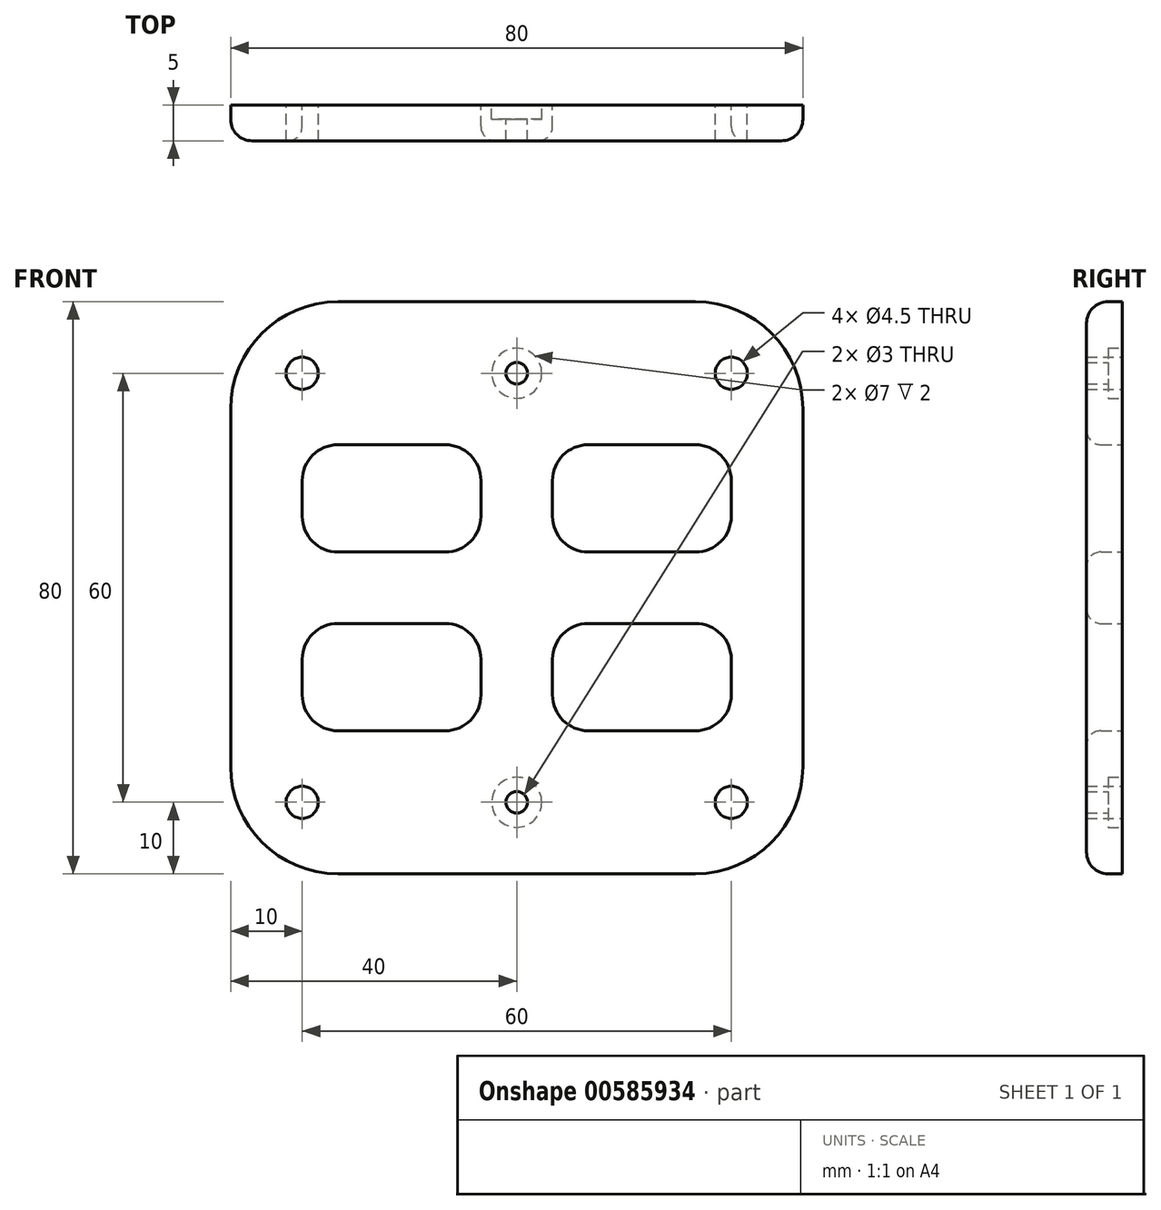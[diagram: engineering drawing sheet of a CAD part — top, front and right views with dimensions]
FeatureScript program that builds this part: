
annotation { "Feature Type Name" : "Feature", "Feature Type Description" : "" }
export const myFeature = defineFeature(function(context is Context, id is Id, definition is map)
    precondition{}
    {
        {
            var Q0;
            Q0=qCreatedBy(makeId("Front.planeOp"),FACE);
            var sketch = newSketch(context, id + "F0", { "sketchPlane" : qUnion([Q0])});
            skLineSegment(sketch, "E0.bottom", {"start": v(-40, 40) * mm, "end": v(40, 40) * mm});
            skLineSegment(sketch, "E0.top", {"start": v(-40, -40) * mm, "end": v(40, -40) * mm});
            skLineSegment(sketch, "E0.left", {"start": v(-40, 40) * mm, "end": v(-40, -40) * mm});
            skLineSegment(sketch, "E0.right", {"start": v(40, 40) * mm, "end": v(40, -40) * mm});
            skCircle(sketch, "E1", {"center": v(-30, 30) * mm, "radius": 2.25 * mm});
            skCircle(sketch, "E2", {"center": v(0, 30) * mm, "radius": 1.5 * mm});
            skCircle(sketch, "E3", {"center": v(30, 30) * mm, "radius": 2.25 * mm});
            skCircle(sketch, "E4", {"center": v(-30, -30) * mm, "radius": 2.25 * mm});
            skCircle(sketch, "E5", {"center": v(0, -30) * mm, "radius": 1.5 * mm});
            skCircle(sketch, "E6", {"center": v(30, -30) * mm, "radius": 2.25 * mm});
            skLineSegment(sketch, "E7.bottom", {"start": v(-30, 20) * mm, "end": v(-5, 20) * mm});
            skLineSegment(sketch, "E7.top", {"start": v(-30, 5) * mm, "end": v(-5, 5) * mm});
            skLineSegment(sketch, "E7.left", {"start": v(-30, 20) * mm, "end": v(-30, 5) * mm});
            skLineSegment(sketch, "E7.right", {"start": v(-5, 20) * mm, "end": v(-5, 5) * mm});
            skLineSegment(sketch, "E8.bottom", {"start": v(-30, -5) * mm, "end": v(-5, -5) * mm});
            skLineSegment(sketch, "E8.top", {"start": v(-30, -20) * mm, "end": v(-5, -20) * mm});
            skLineSegment(sketch, "E8.left", {"start": v(-30, -5) * mm, "end": v(-30, -20) * mm});
            skLineSegment(sketch, "E8.right", {"start": v(-5, -5) * mm, "end": v(-5, -20) * mm});
            skLineSegment(sketch, "E9.bottom", {"start": v(5, -5) * mm, "end": v(30, -5) * mm});
            skLineSegment(sketch, "E9.top", {"start": v(5, -20) * mm, "end": v(30, -20) * mm});
            skLineSegment(sketch, "E9.left", {"start": v(5, -5) * mm, "end": v(5, -20) * mm});
            skLineSegment(sketch, "E9.right", {"start": v(30, -5) * mm, "end": v(30, -20) * mm});
            skLineSegment(sketch, "E10.bottom", {"start": v(5, 20) * mm, "end": v(30, 20) * mm});
            skLineSegment(sketch, "E10.top", {"start": v(5, 5) * mm, "end": v(30, 5) * mm});
            skLineSegment(sketch, "E10.left", {"start": v(5, 20) * mm, "end": v(5, 5) * mm});
            skLineSegment(sketch, "E10.right", {"start": v(30, 20) * mm, "end": v(30, 5) * mm});
            skSolve(sketch);
        }
        {
            var Q0;
            Q0 = qSketchRegion(id + "F0", true);
            extrude(context, id + "F1", {"entities" : qUnion([Q0]), "depth" : 5 * mm, "offsetDistance" : 25 * mm});
        }
        {
            var Q0;
            Q0=makeQuery(id+"F1.opExtrude","SWEPT_EDGE",EDGE,{"disambiguationData":[OSD([sQuery(id+"F0.wireOp",EDGE,"E10.top"),sQuery(id+"F0.wireOp",EDGE,"E10.right")])]});
            var Q1;
            Q1=makeQuery(id+"F1.opExtrude","SWEPT_EDGE",EDGE,{"disambiguationData":[OSD([sQuery(id+"F0.wireOp",EDGE,"E10.bottom"),sQuery(id+"F0.wireOp",EDGE,"E10.right")])]});
            var Q2;
            Q2=makeQuery(id+"F1.opExtrude","SWEPT_EDGE",EDGE,{"disambiguationData":[OSD([sQuery(id+"F0.wireOp",EDGE,"E10.bottom"),sQuery(id+"F0.wireOp",EDGE,"E10.left")])]});
            var Q3;
            Q3=makeQuery(id+"F1.opExtrude","SWEPT_EDGE",EDGE,{"disambiguationData":[OSD([sQuery(id+"F0.wireOp",EDGE,"E10.top"),sQuery(id+"F0.wireOp",EDGE,"E10.left")])]});
            fillet(context, id + "F2", {"entities" : qUnion([Q0, Q1, Q2, Q3]), "radius" : 5 * mm, "tangentPropagation" : true, "allowEdgeOverflow" : false});
        }
        {
            var Q0;
            Q0=makeQuery(id+"F1.opExtrude","SWEPT_EDGE",EDGE,{"disambiguationData":[OSD([sQuery(id+"F0.wireOp",EDGE,"E7.bottom"),sQuery(id+"F0.wireOp",EDGE,"E7.left")])]});
            var Q1;
            Q1=makeQuery(id+"F1.opExtrude","SWEPT_EDGE",EDGE,{"disambiguationData":[OSD([sQuery(id+"F0.wireOp",EDGE,"E7.top"),sQuery(id+"F0.wireOp",EDGE,"E7.left")])]});
            var Q2;
            Q2=makeQuery(id+"F1.opExtrude","SWEPT_EDGE",EDGE,{"disambiguationData":[OSD([sQuery(id+"F0.wireOp",EDGE,"E7.top"),sQuery(id+"F0.wireOp",EDGE,"E7.right")])]});
            var Q3;
            Q3=makeQuery(id+"F1.opExtrude","SWEPT_EDGE",EDGE,{"disambiguationData":[OSD([sQuery(id+"F0.wireOp",EDGE,"E7.bottom"),sQuery(id+"F0.wireOp",EDGE,"E7.right")])]});
            fillet(context, id + "F3", {"entities" : qUnion([Q0, Q1, Q2, Q3]), "radius" : 5 * mm, "tangentPropagation" : true, "allowEdgeOverflow" : false});
        }
        {
            var Q0;
            Q0=makeQuery(id+"F1.opExtrude","SWEPT_EDGE",EDGE,{"disambiguationData":[OSD([sQuery(id+"F0.wireOp",EDGE,"E8.bottom"),sQuery(id+"F0.wireOp",EDGE,"E8.right")])]});
            var Q1;
            Q1=makeQuery(id+"F1.opExtrude","SWEPT_EDGE",EDGE,{"disambiguationData":[OSD([sQuery(id+"F0.wireOp",EDGE,"E9.bottom"),sQuery(id+"F0.wireOp",EDGE,"E9.right")])]});
            var Q2;
            Q2=makeQuery(id+"F1.opExtrude","SWEPT_EDGE",EDGE,{"disambiguationData":[OSD([sQuery(id+"F0.wireOp",EDGE,"E9.bottom"),sQuery(id+"F0.wireOp",EDGE,"E9.left")])]});
            var Q3;
            Q3=makeQuery(id+"F1.opExtrude","SWEPT_EDGE",EDGE,{"disambiguationData":[OSD([sQuery(id+"F0.wireOp",EDGE,"E8.bottom"),sQuery(id+"F0.wireOp",EDGE,"E8.left")])]});
            var Q4;
            Q4=makeQuery(id+"F1.opExtrude","SWEPT_EDGE",EDGE,{"disambiguationData":[OSD([sQuery(id+"F0.wireOp",EDGE,"E9.top"),sQuery(id+"F0.wireOp",EDGE,"E9.right")])]});
            var Q5;
            Q5=makeQuery(id+"F1.opExtrude","SWEPT_EDGE",EDGE,{"disambiguationData":[OSD([sQuery(id+"F0.wireOp",EDGE,"E8.top"),sQuery(id+"F0.wireOp",EDGE,"E8.right")])]});
            var Q6;
            Q6=makeQuery(id+"F1.opExtrude","SWEPT_EDGE",EDGE,{"disambiguationData":[OSD([sQuery(id+"F0.wireOp",EDGE,"E9.top"),sQuery(id+"F0.wireOp",EDGE,"E9.left")])]});
            var Q7;
            Q7=makeQuery(id+"F1.opExtrude","SWEPT_EDGE",EDGE,{"disambiguationData":[OSD([sQuery(id+"F0.wireOp",EDGE,"E8.top"),sQuery(id+"F0.wireOp",EDGE,"E8.left")])]});
            fillet(context, id + "F4", {"entities" : qUnion([Q0, Q1, Q2, Q3, Q4, Q5, Q6, Q7]), "radius" : 5 * mm, "tangentPropagation" : true, "allowEdgeOverflow" : false});
        }
        {
            var Q0;
            Q0=makeQuery(id+"F1.opExtrude","SWEPT_EDGE",EDGE,{"disambiguationData":[OSD([sQuery(id+"F0.wireOp",EDGE,"E0.top"),sQuery(id+"F0.wireOp",EDGE,"E0.right")])]});
            var Q1;
            Q1=makeQuery(id+"F1.opExtrude","SWEPT_EDGE",EDGE,{"disambiguationData":[OSD([sQuery(id+"F0.wireOp",EDGE,"E0.bottom"),sQuery(id+"F0.wireOp",EDGE,"E0.right")])]});
            var Q2;
            Q2=makeQuery(id+"F1.opExtrude","SWEPT_EDGE",EDGE,{"disambiguationData":[OSD([sQuery(id+"F0.wireOp",EDGE,"E0.bottom"),sQuery(id+"F0.wireOp",EDGE,"E0.left")])]});
            var Q3;
            Q3=makeQuery(id+"F1.opExtrude","SWEPT_EDGE",EDGE,{"disambiguationData":[OSD([sQuery(id+"F0.wireOp",EDGE,"E0.top"),sQuery(id+"F0.wireOp",EDGE,"E0.left")])]});
            fillet(context, id + "F5", {"entities" : qUnion([Q0, Q1, Q2, Q3]), "radius" : 15 * mm, "tangentPropagation" : true, "allowEdgeOverflow" : false});
        }
        {
            var Q0;
            {var subQ0=sQuery(id+"F0.wireOp",EDGE,"E0.right");var subQ1=sQuery(id+"F0.wireOp",EDGE,"E0.bottom");Q0=makeQuery(id+"F5.opFillet","BLEND_EDGE",EDGE,{"blendedFrom":[makeQuery(id+"F1.opExtrude","SWEPT_EDGE",EDGE,{"disambiguationData":[OSD([subQ1,subQ0])]}),makeQuery(id+"F1.opExtrude","CAP_FACE",FACE,{"disambiguationData":[OSD([subQ1,sQuery(id+"F0.wireOp",EDGE,"E0.top"),sQuery(id+"F0.wireOp",EDGE,"E0.left"),subQ0,sQuery(id+"F0.wireOp",EDGE,"E1"),sQuery(id+"F0.wireOp",EDGE,"E2"),sQuery(id+"F0.wireOp",EDGE,"E3"),sQuery(id+"F0.wireOp",EDGE,"E4"),sQuery(id+"F0.wireOp",EDGE,"E5"),sQuery(id+"F0.wireOp",EDGE,"E6"),sQuery(id+"F0.wireOp",EDGE,"E7.bottom"),sQuery(id+"F0.wireOp",EDGE,"E7.top"),sQuery(id+"F0.wireOp",EDGE,"E7.left"),sQuery(id+"F0.wireOp",EDGE,"E7.right"),sQuery(id+"F0.wireOp",EDGE,"E8.bottom"),sQuery(id+"F0.wireOp",EDGE,"E8.top"),sQuery(id+"F0.wireOp",EDGE,"E8.left"),sQuery(id+"F0.wireOp",EDGE,"E8.right"),sQuery(id+"F0.wireOp",EDGE,"E9.bottom"),sQuery(id+"F0.wireOp",EDGE,"E9.top"),sQuery(id+"F0.wireOp",EDGE,"E9.left"),sQuery(id+"F0.wireOp",EDGE,"E9.right"),sQuery(id+"F0.wireOp",EDGE,"E10.bottom"),sQuery(id+"F0.wireOp",EDGE,"E10.top"),sQuery(id+"F0.wireOp",EDGE,"E10.left"),sQuery(id+"F0.wireOp",EDGE,"E10.right")])],"isStart":false})],"blendedInto":[makeQuery(id+"F1.opExtrude","CAP_FACE",FACE,{"disambiguationData":[OSD([subQ1,sQuery(id+"F0.wireOp",EDGE,"E0.top"),sQuery(id+"F0.wireOp",EDGE,"E0.left"),subQ0,sQuery(id+"F0.wireOp",EDGE,"E1"),sQuery(id+"F0.wireOp",EDGE,"E2"),sQuery(id+"F0.wireOp",EDGE,"E3"),sQuery(id+"F0.wireOp",EDGE,"E4"),sQuery(id+"F0.wireOp",EDGE,"E5"),sQuery(id+"F0.wireOp",EDGE,"E6"),sQuery(id+"F0.wireOp",EDGE,"E7.bottom"),sQuery(id+"F0.wireOp",EDGE,"E7.top"),sQuery(id+"F0.wireOp",EDGE,"E7.left"),sQuery(id+"F0.wireOp",EDGE,"E7.right"),sQuery(id+"F0.wireOp",EDGE,"E8.bottom"),sQuery(id+"F0.wireOp",EDGE,"E8.top"),sQuery(id+"F0.wireOp",EDGE,"E8.left"),sQuery(id+"F0.wireOp",EDGE,"E8.right"),sQuery(id+"F0.wireOp",EDGE,"E9.bottom"),sQuery(id+"F0.wireOp",EDGE,"E9.top"),sQuery(id+"F0.wireOp",EDGE,"E9.left"),sQuery(id+"F0.wireOp",EDGE,"E9.right"),sQuery(id+"F0.wireOp",EDGE,"E10.bottom"),sQuery(id+"F0.wireOp",EDGE,"E10.top"),sQuery(id+"F0.wireOp",EDGE,"E10.left"),sQuery(id+"F0.wireOp",EDGE,"E10.right")])],"isStart":false})]});}
            fillet(context, id + "F6", {"entities" : qUnion([Q0]), "radius" : 3 * mm, "tangentPropagation" : true, "allowEdgeOverflow" : false});
        }
        {
            var Q0;
            {var subQ0=sQuery(id+"F0.wireOp",EDGE,"E10.left");var subQ1=sQuery(id+"F0.wireOp",EDGE,"E10.bottom");Q0=makeQuery(id+"F2.opFillet","BLEND_EDGE",EDGE,{"blendedFrom":[makeQuery(id+"F1.opExtrude","SWEPT_EDGE",EDGE,{"disambiguationData":[OSD([subQ1,subQ0])]}),makeQuery(id+"F1.opExtrude","CAP_FACE",FACE,{"disambiguationData":[OSD([sQuery(id+"F0.wireOp",EDGE,"E0.bottom"),sQuery(id+"F0.wireOp",EDGE,"E0.top"),sQuery(id+"F0.wireOp",EDGE,"E0.left"),sQuery(id+"F0.wireOp",EDGE,"E0.right"),sQuery(id+"F0.wireOp",EDGE,"E1"),sQuery(id+"F0.wireOp",EDGE,"E2"),sQuery(id+"F0.wireOp",EDGE,"E3"),sQuery(id+"F0.wireOp",EDGE,"E4"),sQuery(id+"F0.wireOp",EDGE,"E5"),sQuery(id+"F0.wireOp",EDGE,"E6"),sQuery(id+"F0.wireOp",EDGE,"E7.bottom"),sQuery(id+"F0.wireOp",EDGE,"E7.top"),sQuery(id+"F0.wireOp",EDGE,"E7.left"),sQuery(id+"F0.wireOp",EDGE,"E7.right"),sQuery(id+"F0.wireOp",EDGE,"E8.bottom"),sQuery(id+"F0.wireOp",EDGE,"E8.top"),sQuery(id+"F0.wireOp",EDGE,"E8.left"),sQuery(id+"F0.wireOp",EDGE,"E8.right"),sQuery(id+"F0.wireOp",EDGE,"E9.bottom"),sQuery(id+"F0.wireOp",EDGE,"E9.top"),sQuery(id+"F0.wireOp",EDGE,"E9.left"),sQuery(id+"F0.wireOp",EDGE,"E9.right"),subQ1,sQuery(id+"F0.wireOp",EDGE,"E10.top"),subQ0,sQuery(id+"F0.wireOp",EDGE,"E10.right")])],"isStart":false})],"blendedInto":[makeQuery(id+"F1.opExtrude","CAP_FACE",FACE,{"disambiguationData":[OSD([sQuery(id+"F0.wireOp",EDGE,"E0.bottom"),sQuery(id+"F0.wireOp",EDGE,"E0.top"),sQuery(id+"F0.wireOp",EDGE,"E0.left"),sQuery(id+"F0.wireOp",EDGE,"E0.right"),sQuery(id+"F0.wireOp",EDGE,"E1"),sQuery(id+"F0.wireOp",EDGE,"E2"),sQuery(id+"F0.wireOp",EDGE,"E3"),sQuery(id+"F0.wireOp",EDGE,"E4"),sQuery(id+"F0.wireOp",EDGE,"E5"),sQuery(id+"F0.wireOp",EDGE,"E6"),sQuery(id+"F0.wireOp",EDGE,"E7.bottom"),sQuery(id+"F0.wireOp",EDGE,"E7.top"),sQuery(id+"F0.wireOp",EDGE,"E7.left"),sQuery(id+"F0.wireOp",EDGE,"E7.right"),sQuery(id+"F0.wireOp",EDGE,"E8.bottom"),sQuery(id+"F0.wireOp",EDGE,"E8.top"),sQuery(id+"F0.wireOp",EDGE,"E8.left"),sQuery(id+"F0.wireOp",EDGE,"E8.right"),sQuery(id+"F0.wireOp",EDGE,"E9.bottom"),sQuery(id+"F0.wireOp",EDGE,"E9.top"),sQuery(id+"F0.wireOp",EDGE,"E9.left"),sQuery(id+"F0.wireOp",EDGE,"E9.right"),subQ1,sQuery(id+"F0.wireOp",EDGE,"E10.top"),subQ0,sQuery(id+"F0.wireOp",EDGE,"E10.right")])],"isStart":false})]});}
            var Q1;
            {var subQ0=sQuery(id+"F0.wireOp",EDGE,"E9.left");var subQ1=sQuery(id+"F0.wireOp",EDGE,"E9.bottom");Q1=makeQuery(id+"F4.opFillet","BLEND_EDGE",EDGE,{"blendedFrom":[makeQuery(id+"F1.opExtrude","SWEPT_EDGE",EDGE,{"disambiguationData":[OSD([subQ1,subQ0])]}),makeQuery(id+"F1.opExtrude","CAP_FACE",FACE,{"disambiguationData":[OSD([sQuery(id+"F0.wireOp",EDGE,"E0.bottom"),sQuery(id+"F0.wireOp",EDGE,"E0.top"),sQuery(id+"F0.wireOp",EDGE,"E0.left"),sQuery(id+"F0.wireOp",EDGE,"E0.right"),sQuery(id+"F0.wireOp",EDGE,"E1"),sQuery(id+"F0.wireOp",EDGE,"E2"),sQuery(id+"F0.wireOp",EDGE,"E3"),sQuery(id+"F0.wireOp",EDGE,"E4"),sQuery(id+"F0.wireOp",EDGE,"E5"),sQuery(id+"F0.wireOp",EDGE,"E6"),sQuery(id+"F0.wireOp",EDGE,"E7.bottom"),sQuery(id+"F0.wireOp",EDGE,"E7.top"),sQuery(id+"F0.wireOp",EDGE,"E7.left"),sQuery(id+"F0.wireOp",EDGE,"E7.right"),sQuery(id+"F0.wireOp",EDGE,"E8.bottom"),sQuery(id+"F0.wireOp",EDGE,"E8.top"),sQuery(id+"F0.wireOp",EDGE,"E8.left"),sQuery(id+"F0.wireOp",EDGE,"E8.right"),subQ1,sQuery(id+"F0.wireOp",EDGE,"E9.top"),subQ0,sQuery(id+"F0.wireOp",EDGE,"E9.right"),sQuery(id+"F0.wireOp",EDGE,"E10.bottom"),sQuery(id+"F0.wireOp",EDGE,"E10.top"),sQuery(id+"F0.wireOp",EDGE,"E10.left"),sQuery(id+"F0.wireOp",EDGE,"E10.right")])],"isStart":false})],"blendedInto":[makeQuery(id+"F1.opExtrude","CAP_FACE",FACE,{"disambiguationData":[OSD([sQuery(id+"F0.wireOp",EDGE,"E0.bottom"),sQuery(id+"F0.wireOp",EDGE,"E0.top"),sQuery(id+"F0.wireOp",EDGE,"E0.left"),sQuery(id+"F0.wireOp",EDGE,"E0.right"),sQuery(id+"F0.wireOp",EDGE,"E1"),sQuery(id+"F0.wireOp",EDGE,"E2"),sQuery(id+"F0.wireOp",EDGE,"E3"),sQuery(id+"F0.wireOp",EDGE,"E4"),sQuery(id+"F0.wireOp",EDGE,"E5"),sQuery(id+"F0.wireOp",EDGE,"E6"),sQuery(id+"F0.wireOp",EDGE,"E7.bottom"),sQuery(id+"F0.wireOp",EDGE,"E7.top"),sQuery(id+"F0.wireOp",EDGE,"E7.left"),sQuery(id+"F0.wireOp",EDGE,"E7.right"),sQuery(id+"F0.wireOp",EDGE,"E8.bottom"),sQuery(id+"F0.wireOp",EDGE,"E8.top"),sQuery(id+"F0.wireOp",EDGE,"E8.left"),sQuery(id+"F0.wireOp",EDGE,"E8.right"),subQ1,sQuery(id+"F0.wireOp",EDGE,"E9.top"),subQ0,sQuery(id+"F0.wireOp",EDGE,"E9.right"),sQuery(id+"F0.wireOp",EDGE,"E10.bottom"),sQuery(id+"F0.wireOp",EDGE,"E10.top"),sQuery(id+"F0.wireOp",EDGE,"E10.left"),sQuery(id+"F0.wireOp",EDGE,"E10.right")])],"isStart":false})]});}
            var Q2;
            {var subQ0=sQuery(id+"F0.wireOp",EDGE,"E7.left");var subQ1=sQuery(id+"F0.wireOp",EDGE,"E7.bottom");Q2=makeQuery(id+"F3.opFillet","BLEND_EDGE",EDGE,{"blendedFrom":[makeQuery(id+"F1.opExtrude","SWEPT_EDGE",EDGE,{"disambiguationData":[OSD([subQ1,subQ0])]}),makeQuery(id+"F1.opExtrude","CAP_FACE",FACE,{"disambiguationData":[OSD([sQuery(id+"F0.wireOp",EDGE,"E0.bottom"),sQuery(id+"F0.wireOp",EDGE,"E0.top"),sQuery(id+"F0.wireOp",EDGE,"E0.left"),sQuery(id+"F0.wireOp",EDGE,"E0.right"),sQuery(id+"F0.wireOp",EDGE,"E1"),sQuery(id+"F0.wireOp",EDGE,"E2"),sQuery(id+"F0.wireOp",EDGE,"E3"),sQuery(id+"F0.wireOp",EDGE,"E4"),sQuery(id+"F0.wireOp",EDGE,"E5"),sQuery(id+"F0.wireOp",EDGE,"E6"),subQ1,sQuery(id+"F0.wireOp",EDGE,"E7.top"),subQ0,sQuery(id+"F0.wireOp",EDGE,"E7.right"),sQuery(id+"F0.wireOp",EDGE,"E8.bottom"),sQuery(id+"F0.wireOp",EDGE,"E8.top"),sQuery(id+"F0.wireOp",EDGE,"E8.left"),sQuery(id+"F0.wireOp",EDGE,"E8.right"),sQuery(id+"F0.wireOp",EDGE,"E9.bottom"),sQuery(id+"F0.wireOp",EDGE,"E9.top"),sQuery(id+"F0.wireOp",EDGE,"E9.left"),sQuery(id+"F0.wireOp",EDGE,"E9.right"),sQuery(id+"F0.wireOp",EDGE,"E10.bottom"),sQuery(id+"F0.wireOp",EDGE,"E10.top"),sQuery(id+"F0.wireOp",EDGE,"E10.left"),sQuery(id+"F0.wireOp",EDGE,"E10.right")])],"isStart":false})],"blendedInto":[makeQuery(id+"F1.opExtrude","CAP_FACE",FACE,{"disambiguationData":[OSD([sQuery(id+"F0.wireOp",EDGE,"E0.bottom"),sQuery(id+"F0.wireOp",EDGE,"E0.top"),sQuery(id+"F0.wireOp",EDGE,"E0.left"),sQuery(id+"F0.wireOp",EDGE,"E0.right"),sQuery(id+"F0.wireOp",EDGE,"E1"),sQuery(id+"F0.wireOp",EDGE,"E2"),sQuery(id+"F0.wireOp",EDGE,"E3"),sQuery(id+"F0.wireOp",EDGE,"E4"),sQuery(id+"F0.wireOp",EDGE,"E5"),sQuery(id+"F0.wireOp",EDGE,"E6"),subQ1,sQuery(id+"F0.wireOp",EDGE,"E7.top"),subQ0,sQuery(id+"F0.wireOp",EDGE,"E7.right"),sQuery(id+"F0.wireOp",EDGE,"E8.bottom"),sQuery(id+"F0.wireOp",EDGE,"E8.top"),sQuery(id+"F0.wireOp",EDGE,"E8.left"),sQuery(id+"F0.wireOp",EDGE,"E8.right"),sQuery(id+"F0.wireOp",EDGE,"E9.bottom"),sQuery(id+"F0.wireOp",EDGE,"E9.top"),sQuery(id+"F0.wireOp",EDGE,"E9.left"),sQuery(id+"F0.wireOp",EDGE,"E9.right"),sQuery(id+"F0.wireOp",EDGE,"E10.bottom"),sQuery(id+"F0.wireOp",EDGE,"E10.top"),sQuery(id+"F0.wireOp",EDGE,"E10.left"),sQuery(id+"F0.wireOp",EDGE,"E10.right")])],"isStart":false})]});}
            var Q3;
            {var subQ0=sQuery(id+"F0.wireOp",EDGE,"E8.left");var subQ1=sQuery(id+"F0.wireOp",EDGE,"E8.bottom");Q3=makeQuery(id+"F4.opFillet","BLEND_EDGE",EDGE,{"blendedFrom":[makeQuery(id+"F1.opExtrude","SWEPT_EDGE",EDGE,{"disambiguationData":[OSD([subQ1,subQ0])]}),makeQuery(id+"F1.opExtrude","CAP_FACE",FACE,{"disambiguationData":[OSD([sQuery(id+"F0.wireOp",EDGE,"E0.bottom"),sQuery(id+"F0.wireOp",EDGE,"E0.top"),sQuery(id+"F0.wireOp",EDGE,"E0.left"),sQuery(id+"F0.wireOp",EDGE,"E0.right"),sQuery(id+"F0.wireOp",EDGE,"E1"),sQuery(id+"F0.wireOp",EDGE,"E2"),sQuery(id+"F0.wireOp",EDGE,"E3"),sQuery(id+"F0.wireOp",EDGE,"E4"),sQuery(id+"F0.wireOp",EDGE,"E5"),sQuery(id+"F0.wireOp",EDGE,"E6"),sQuery(id+"F0.wireOp",EDGE,"E7.bottom"),sQuery(id+"F0.wireOp",EDGE,"E7.top"),sQuery(id+"F0.wireOp",EDGE,"E7.left"),sQuery(id+"F0.wireOp",EDGE,"E7.right"),subQ1,sQuery(id+"F0.wireOp",EDGE,"E8.top"),subQ0,sQuery(id+"F0.wireOp",EDGE,"E8.right"),sQuery(id+"F0.wireOp",EDGE,"E9.bottom"),sQuery(id+"F0.wireOp",EDGE,"E9.top"),sQuery(id+"F0.wireOp",EDGE,"E9.left"),sQuery(id+"F0.wireOp",EDGE,"E9.right"),sQuery(id+"F0.wireOp",EDGE,"E10.bottom"),sQuery(id+"F0.wireOp",EDGE,"E10.top"),sQuery(id+"F0.wireOp",EDGE,"E10.left"),sQuery(id+"F0.wireOp",EDGE,"E10.right")])],"isStart":false})],"blendedInto":[makeQuery(id+"F1.opExtrude","CAP_FACE",FACE,{"disambiguationData":[OSD([sQuery(id+"F0.wireOp",EDGE,"E0.bottom"),sQuery(id+"F0.wireOp",EDGE,"E0.top"),sQuery(id+"F0.wireOp",EDGE,"E0.left"),sQuery(id+"F0.wireOp",EDGE,"E0.right"),sQuery(id+"F0.wireOp",EDGE,"E1"),sQuery(id+"F0.wireOp",EDGE,"E2"),sQuery(id+"F0.wireOp",EDGE,"E3"),sQuery(id+"F0.wireOp",EDGE,"E4"),sQuery(id+"F0.wireOp",EDGE,"E5"),sQuery(id+"F0.wireOp",EDGE,"E6"),sQuery(id+"F0.wireOp",EDGE,"E7.bottom"),sQuery(id+"F0.wireOp",EDGE,"E7.top"),sQuery(id+"F0.wireOp",EDGE,"E7.left"),sQuery(id+"F0.wireOp",EDGE,"E7.right"),subQ1,sQuery(id+"F0.wireOp",EDGE,"E8.top"),subQ0,sQuery(id+"F0.wireOp",EDGE,"E8.right"),sQuery(id+"F0.wireOp",EDGE,"E9.bottom"),sQuery(id+"F0.wireOp",EDGE,"E9.top"),sQuery(id+"F0.wireOp",EDGE,"E9.left"),sQuery(id+"F0.wireOp",EDGE,"E9.right"),sQuery(id+"F0.wireOp",EDGE,"E10.bottom"),sQuery(id+"F0.wireOp",EDGE,"E10.top"),sQuery(id+"F0.wireOp",EDGE,"E10.left"),sQuery(id+"F0.wireOp",EDGE,"E10.right")])],"isStart":false})]});}
            fillet(context, id + "F7", {"entities" : qUnion([Q0, Q1, Q2, Q3]), "radius" : 2 * mm, "tangentPropagation" : true, "allowEdgeOverflow" : false});
        }
        {
            var Q0;
            Q0=makeQuery(id+"F1.opExtrude","CAP_FACE",FACE,{"disambiguationData":[OSD([sQuery(id+"F0.wireOp",EDGE,"E0.bottom"),sQuery(id+"F0.wireOp",EDGE,"E0.top"),sQuery(id+"F0.wireOp",EDGE,"E0.left"),sQuery(id+"F0.wireOp",EDGE,"E0.right"),sQuery(id+"F0.wireOp",EDGE,"E1"),sQuery(id+"F0.wireOp",EDGE,"E2"),sQuery(id+"F0.wireOp",EDGE,"E3"),sQuery(id+"F0.wireOp",EDGE,"E4"),sQuery(id+"F0.wireOp",EDGE,"E5"),sQuery(id+"F0.wireOp",EDGE,"E6"),sQuery(id+"F0.wireOp",EDGE,"E7.bottom"),sQuery(id+"F0.wireOp",EDGE,"E7.top"),sQuery(id+"F0.wireOp",EDGE,"E7.left"),sQuery(id+"F0.wireOp",EDGE,"E7.right"),sQuery(id+"F0.wireOp",EDGE,"E8.bottom"),sQuery(id+"F0.wireOp",EDGE,"E8.top"),sQuery(id+"F0.wireOp",EDGE,"E8.left"),sQuery(id+"F0.wireOp",EDGE,"E8.right"),sQuery(id+"F0.wireOp",EDGE,"E9.bottom"),sQuery(id+"F0.wireOp",EDGE,"E9.top"),sQuery(id+"F0.wireOp",EDGE,"E9.left"),sQuery(id+"F0.wireOp",EDGE,"E9.right"),sQuery(id+"F0.wireOp",EDGE,"E10.bottom"),sQuery(id+"F0.wireOp",EDGE,"E10.top"),sQuery(id+"F0.wireOp",EDGE,"E10.left"),sQuery(id+"F0.wireOp",EDGE,"E10.right")])],"isStart":true});
            var sketch = newSketch(context, id + "F8", { "sketchPlane" : qUnion([Q0])});
            skCircle(sketch, "E11", {"center": v(0, 30) * mm, "radius": 3.5 * mm});
            skCircle(sketch, "E12", {"center": v(0, -30) * mm, "radius": 3.5 * mm});
            skSolve(sketch);
        }
        {
            var Q0;
            Q0 = qSketchRegion(id + "F8", true);
            extrude(context, id + "F9", {"entities" : qUnion([Q0]), "operationType" : NewBodyOperationType.REMOVE, "oppositeDirection" : true, "depth" : 2 * mm, "offsetDistance" : 25 * mm});
        }
    });
